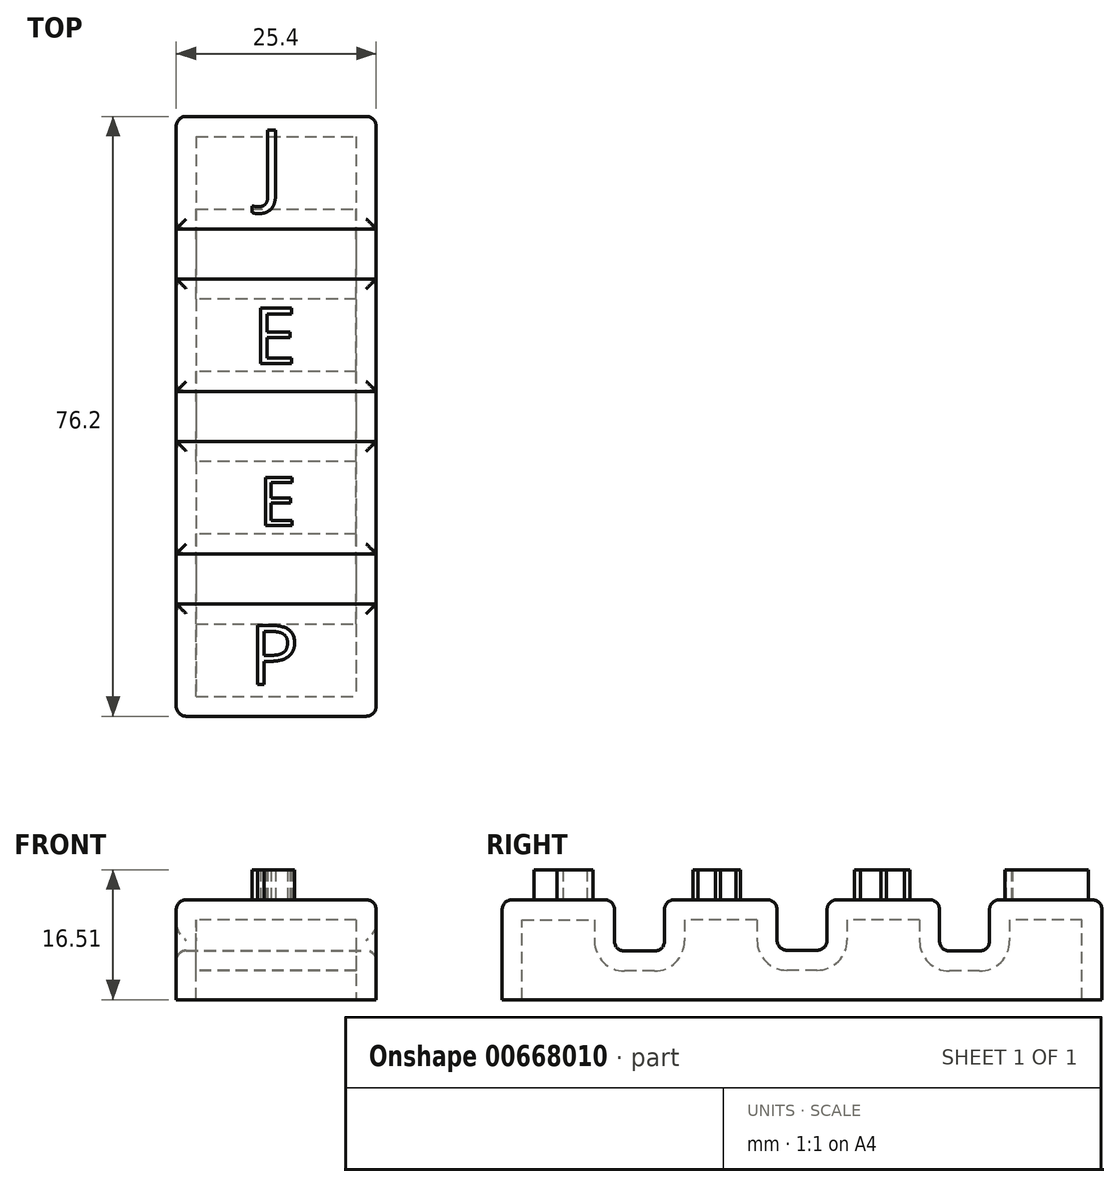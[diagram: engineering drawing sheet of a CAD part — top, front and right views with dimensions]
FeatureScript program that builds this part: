
annotation { "Feature Type Name" : "Feature", "Feature Type Description" : "" }
export const myFeature = defineFeature(function(context is Context, id is Id, definition is map)
    precondition{}
    {
        {
            var Q0;
            Q0=qCreatedBy(makeId("Top.planeOp"),FACE);
            var sketch = newSketch(context, id + "F0", { "sketchPlane" : qUnion([Q0])});
            skLineSegment(sketch, "E0.bottom", {"start": v(-12.7, 38.1) * mm, "end": v(12.7, 38.1) * mm});
            skLineSegment(sketch, "E0.top", {"start": v(-12.7, -38.1) * mm, "end": v(12.7, -38.1) * mm});
            skLineSegment(sketch, "E0.left", {"start": v(-12.7, 38.1) * mm, "end": v(-12.7, -38.1) * mm});
            skLineSegment(sketch, "E0.right", {"start": v(12.7, 38.1) * mm, "end": v(12.7, -38.1) * mm});
            skPoint(sketch, "E0.middle", {"position": v(0, 0) * mm});
            skSolve(sketch);
        }
        {
            var Q0;
            Q0 = qSketchRegion(id + "F0", true);
            extrude(context, id + "F1", {"entities" : qUnion([Q0]), "depth" : 12.7 * mm, "offsetDistance" : 25.4 * mm});
        }
        {
            var Q0;
            Q0=makeQuery(id+"F1.opExtrude","SWEPT_FACE",FACE,{"disambiguationData":[OSD([sQuery(id+"F0.wireOp",EDGE,"E0.right")])]});
            var sketch = newSketch(context, id + "F2", { "sketchPlane" : qUnion([Q0])});
            skLineSegment(sketch, "E1", {"start": v(-38.1, 6.35) * mm, "end": v(38.1, 6.35) * mm, "construction": true});
            skLineSegment(sketch, "E2.bottom", {"start": v(-3.17, 19.13) * mm, "end": v(3.18, 19.13) * mm});
            skLineSegment(sketch, "E2.top", {"start": v(-3.17, 6.27) * mm, "end": v(3.18, 6.27) * mm});
            skLineSegment(sketch, "E2.left", {"start": v(-3.17, 19.13) * mm, "end": v(-3.17, 6.27) * mm});
            skLineSegment(sketch, "E2.right", {"start": v(3.18, 19.13) * mm, "end": v(3.18, 6.27) * mm});
            skPoint(sketch, "E2.middle", {"position": v(0, 12.7) * mm});
            skLineSegment(sketch, "E3.bottom", {"start": v(17.46, 19.23) * mm, "end": v(23.81, 19.23) * mm});
            skLineSegment(sketch, "E3.top", {"start": v(17.46, 6.17) * mm, "end": v(23.81, 6.17) * mm});
            skLineSegment(sketch, "E3.left", {"start": v(17.46, 19.23) * mm, "end": v(17.46, 6.17) * mm});
            skLineSegment(sketch, "E3.right", {"start": v(23.81, 19.23) * mm, "end": v(23.81, 6.17) * mm});
            skPoint(sketch, "E3.middle", {"position": v(20.64, 12.7) * mm});
            skLineSegment(sketch, "E4.bottom", {"start": v(-23.83, 19.23) * mm, "end": v(-17.48, 19.23) * mm});
            skLineSegment(sketch, "E4.top", {"start": v(-23.83, 6.17) * mm, "end": v(-17.48, 6.17) * mm});
            skLineSegment(sketch, "E4.left", {"start": v(-23.83, 19.23) * mm, "end": v(-23.83, 6.17) * mm});
            skLineSegment(sketch, "E4.right", {"start": v(-17.48, 19.23) * mm, "end": v(-17.48, 6.17) * mm});
            skPoint(sketch, "E4.middle", {"position": v(-20.65, 12.7) * mm});
            skSolve(sketch);
        }
        {
            var Q0;
            Q0 = qSketchRegion(id + "F2", true);
            extrude(context, id + "F3", {"entities" : qUnion([Q0]), "operationType" : NewBodyOperationType.REMOVE, "endBound" : BoundingType.THROUGH_ALL, "oppositeDirection" : true, "depth" : 25.4 * mm, "offsetDistance" : 25.4 * mm});
        }
        {
            var Q0;
            {var subQ0=sQuery(id+"F0.wireOp",EDGE,"E0.top");var subQ1=sQuery(id+"F0.wireOp",EDGE,"E0.left");var subQ2=sQuery(id+"F0.wireOp",EDGE,"E0.right");Q0=makeQuery(id+"F3.boolean.opBoolean","SPLIT",FACE,{"disambiguationData":[TD([makeQuery(id+"F1.opExtrude","SWEPT_FACE",FACE,{"disambiguationData":[OSD([subQ0])]})])],"derivedFrom":makeQuery(id+"F1.opExtrude","CAP_FACE",FACE,{"disambiguationData":[OSD([sQuery(id+"F0.wireOp",EDGE,"E0.bottom"),subQ0,subQ1,subQ2])],"isStart":false})});}
            var Q1;
            {var subQ0=sQuery(id+"F0.wireOp",EDGE,"E0.left");var subQ1=sQuery(id+"F0.wireOp",EDGE,"E0.right");Q1=makeQuery(id+"F3.boolean.opBoolean","SPLIT",FACE,{"disambiguationData":[TD([makeQuery(id+"F3.opExtrude","SWEPT_FACE",FACE,{"disambiguationData":[OSD([sQuery(id+"F2.wireOp",EDGE,"E2.left")])]})])],"derivedFrom":makeQuery(id+"F1.opExtrude","CAP_FACE",FACE,{"disambiguationData":[OSD([sQuery(id+"F0.wireOp",EDGE,"E0.bottom"),sQuery(id+"F0.wireOp",EDGE,"E0.top"),subQ0,subQ1])],"isStart":false})});}
            var Q2;
            {var subQ0=sQuery(id+"F0.wireOp",EDGE,"E0.left");var subQ1=sQuery(id+"F0.wireOp",EDGE,"E0.right");Q2=makeQuery(id+"F3.boolean.opBoolean","SPLIT",FACE,{"disambiguationData":[TD([makeQuery(id+"F3.opExtrude","SWEPT_FACE",FACE,{"disambiguationData":[OSD([sQuery(id+"F2.wireOp",EDGE,"E2.right")])]})])],"derivedFrom":makeQuery(id+"F1.opExtrude","CAP_FACE",FACE,{"disambiguationData":[OSD([sQuery(id+"F0.wireOp",EDGE,"E0.bottom"),sQuery(id+"F0.wireOp",EDGE,"E0.top"),subQ0,subQ1])],"isStart":false})});}
            var Q3;
            {var subQ0=sQuery(id+"F0.wireOp",EDGE,"E0.bottom");var subQ1=sQuery(id+"F0.wireOp",EDGE,"E0.right");var subQ2=sQuery(id+"F0.wireOp",EDGE,"E0.left");Q3=makeQuery(id+"F3.boolean.opBoolean","SPLIT",FACE,{"disambiguationData":[TD([makeQuery(id+"F1.opExtrude","SWEPT_FACE",FACE,{"disambiguationData":[OSD([subQ0])]})])],"derivedFrom":makeQuery(id+"F1.opExtrude","CAP_FACE",FACE,{"disambiguationData":[OSD([subQ0,sQuery(id+"F0.wireOp",EDGE,"E0.top"),subQ2,subQ1])],"isStart":false})});}
            var Q4;
            Q4=makeQuery(id+"F3.boolean.opBoolean","COPY",FACE,{"derivedFrom":makeQuery(id+"F3.opExtrude","SWEPT_FACE",FACE,{"disambiguationData":[OSD([sQuery(id+"F2.wireOp",EDGE,"E4.top")])]})});
            var Q5;
            Q5=makeQuery(id+"F3.boolean.opBoolean","COPY",FACE,{"derivedFrom":makeQuery(id+"F3.opExtrude","SWEPT_FACE",FACE,{"disambiguationData":[OSD([sQuery(id+"F2.wireOp",EDGE,"E2.top")])]})});
            var Q6;
            Q6=makeQuery(id+"F3.boolean.opBoolean","COPY",FACE,{"derivedFrom":makeQuery(id+"F3.opExtrude","SWEPT_FACE",FACE,{"disambiguationData":[OSD([sQuery(id+"F2.wireOp",EDGE,"E3.top")])]})});
            var Q7;
            Q7=makeQuery(id+"F1.opExtrude","SWEPT_EDGE",EDGE,{"disambiguationData":[OSD([sQuery(id+"F0.wireOp",EDGE,"E0.bottom"),sQuery(id+"F0.wireOp",EDGE,"E0.right")])]});
            var Q8;
            Q8=makeQuery(id+"F1.opExtrude","SWEPT_EDGE",EDGE,{"disambiguationData":[OSD([sQuery(id+"F0.wireOp",EDGE,"E0.bottom"),sQuery(id+"F0.wireOp",EDGE,"E0.left")])]});
            var Q9;
            Q9=makeQuery(id+"F1.opExtrude","SWEPT_EDGE",EDGE,{"disambiguationData":[OSD([sQuery(id+"F0.wireOp",EDGE,"E0.top"),sQuery(id+"F0.wireOp",EDGE,"E0.right")])]});
            var Q10;
            Q10=makeQuery(id+"F1.opExtrude","SWEPT_EDGE",EDGE,{"disambiguationData":[OSD([sQuery(id+"F0.wireOp",EDGE,"E0.top"),sQuery(id+"F0.wireOp",EDGE,"E0.left")])]});
            fillet(context, id + "F4", {"entities" : qUnion([Q0, Q1, Q2, Q3, Q4, Q5, Q6, Q7, Q8, Q9, Q10]), "radius" : 1.27 * mm, "tangentPropagation" : true, "allowEdgeOverflow" : false});
        }
        {
            var Q0;
            Q0=makeQuery(id+"F1.opExtrude","CAP_FACE",FACE,{"disambiguationData":[OSD([sQuery(id+"F0.wireOp",EDGE,"E0.bottom"),sQuery(id+"F0.wireOp",EDGE,"E0.top"),sQuery(id+"F0.wireOp",EDGE,"E0.left"),sQuery(id+"F0.wireOp",EDGE,"E0.right")])],"isStart":true});
            shell(context, id + "F5", {"entities" : qUnion([Q0]), "thickness" : 2.54 * mm});
        }
        {
            var Q0;
            {var subQ0=sQuery(id+"F0.wireOp",EDGE,"E0.bottom");var subQ1=sQuery(id+"F0.wireOp",EDGE,"E0.right");var subQ2=sQuery(id+"F0.wireOp",EDGE,"E0.left");Q0=makeQuery(id+"F3.boolean.opBoolean","SPLIT",FACE,{"disambiguationData":[TD([makeQuery(id+"F1.opExtrude","SWEPT_FACE",FACE,{"disambiguationData":[OSD([subQ0])]})])],"derivedFrom":makeQuery(id+"F1.opExtrude","CAP_FACE",FACE,{"disambiguationData":[OSD([subQ0,sQuery(id+"F0.wireOp",EDGE,"E0.top"),subQ2,subQ1])],"isStart":false})});}
            var sketch = newSketch(context, id + "F6", { "sketchPlane" : qUnion([Q0])});
            skText(sketch, "E5", { "text": "J", "fontName": "OpenSans-Regular.ttf"});
            const initialGuessF6  = {"E5": [-0.00216, 0.02796, 1, 0, 0.00848]};
            skSetInitialGuess(sketch, initialGuessF6);
            skSolve(sketch);
        }
        {
            var Q0;
            Q0 = qSketchRegion(id + "F6", true);
            extrude(context, id + "F7", {"entities" : qUnion([Q0]), "operationType" : NewBodyOperationType.ADD, "depth" : 3.8 * mm, "offsetDistance" : 25.4 * mm});
        }
        {
            var Q0;
            {var subQ0=sQuery(id+"F0.wireOp",EDGE,"E0.left");var subQ1=sQuery(id+"F0.wireOp",EDGE,"E0.right");Q0=makeQuery(id+"F3.boolean.opBoolean","SPLIT",FACE,{"disambiguationData":[TD([makeQuery(id+"F3.opExtrude","SWEPT_FACE",FACE,{"disambiguationData":[OSD([sQuery(id+"F2.wireOp",EDGE,"E2.right")])]})])],"derivedFrom":makeQuery(id+"F1.opExtrude","CAP_FACE",FACE,{"disambiguationData":[OSD([sQuery(id+"F0.wireOp",EDGE,"E0.bottom"),sQuery(id+"F0.wireOp",EDGE,"E0.top"),subQ0,subQ1])],"isStart":false})});}
            var sketch = newSketch(context, id + "F8", { "sketchPlane" : qUnion([Q0])});
            skText(sketch, "E6", { "text": "E", "fontName": "OpenSans-Regular.ttf"});
            const initialGuessF8  = {"E6": [-0.00296, 0.00668, 1, 0, 0.00711]};
            skSetInitialGuess(sketch, initialGuessF8);
            skSolve(sketch);
        }
        {
            var Q0;
            Q0 = qSketchRegion(id + "F8", true);
            extrude(context, id + "F9", {"entities" : qUnion([Q0]), "operationType" : NewBodyOperationType.ADD, "depth" : 3.8 * mm, "offsetDistance" : 25.4 * mm});
        }
        {
            var Q0;
            {var subQ0=sQuery(id+"F0.wireOp",EDGE,"E0.left");var subQ1=sQuery(id+"F0.wireOp",EDGE,"E0.right");Q0=makeQuery(id+"F3.boolean.opBoolean","SPLIT",FACE,{"disambiguationData":[TD([makeQuery(id+"F3.opExtrude","SWEPT_FACE",FACE,{"disambiguationData":[OSD([sQuery(id+"F2.wireOp",EDGE,"E2.left")])]})])],"derivedFrom":makeQuery(id+"F1.opExtrude","CAP_FACE",FACE,{"disambiguationData":[OSD([sQuery(id+"F0.wireOp",EDGE,"E0.bottom"),sQuery(id+"F0.wireOp",EDGE,"E0.top"),subQ0,subQ1])],"isStart":false})});}
            var sketch = newSketch(context, id + "F10", { "sketchPlane" : qUnion([Q0])});
            skText(sketch, "E7", { "text": "E", "fontName": "OpenSans-Regular.ttf"});
            const initialGuessF10  = {"E7": [-0.00221, -0.01387, 1, 0, 0.00613]};
            skSetInitialGuess(sketch, initialGuessF10);
            skSolve(sketch);
        }
        {
            var Q0;
            Q0 = qSketchRegion(id + "F10", true);
            extrude(context, id + "F11", {"entities" : qUnion([Q0]), "operationType" : NewBodyOperationType.ADD, "depth" : 3.8 * mm, "offsetDistance" : 25.4 * mm});
        }
        {
            var Q0;
            {var subQ0=sQuery(id+"F0.wireOp",EDGE,"E0.top");var subQ1=sQuery(id+"F0.wireOp",EDGE,"E0.left");var subQ2=sQuery(id+"F0.wireOp",EDGE,"E0.right");Q0=makeQuery(id+"F3.boolean.opBoolean","SPLIT",FACE,{"disambiguationData":[TD([makeQuery(id+"F1.opExtrude","SWEPT_FACE",FACE,{"disambiguationData":[OSD([subQ0])]})])],"derivedFrom":makeQuery(id+"F1.opExtrude","CAP_FACE",FACE,{"disambiguationData":[OSD([sQuery(id+"F0.wireOp",EDGE,"E0.bottom"),subQ0,subQ1,subQ2])],"isStart":false})});}
            var sketch = newSketch(context, id + "F12", { "sketchPlane" : qUnion([Q0])});
            skText(sketch, "E8", { "text": "P", "fontName": "OpenSans-Regular.ttf"});
            const initialGuessF12  = {"E8": [-0.00342, -0.03406, 1, 0, 0.00754]};
            skSetInitialGuess(sketch, initialGuessF12);
            skSolve(sketch);
        }
        {
            var Q0;
            Q0 = qSketchRegion(id + "F12", true);
            extrude(context, id + "F13", {"entities" : qUnion([Q0]), "operationType" : NewBodyOperationType.ADD, "depth" : 3.8 * mm, "offsetDistance" : 25.4 * mm});
        }
    });
